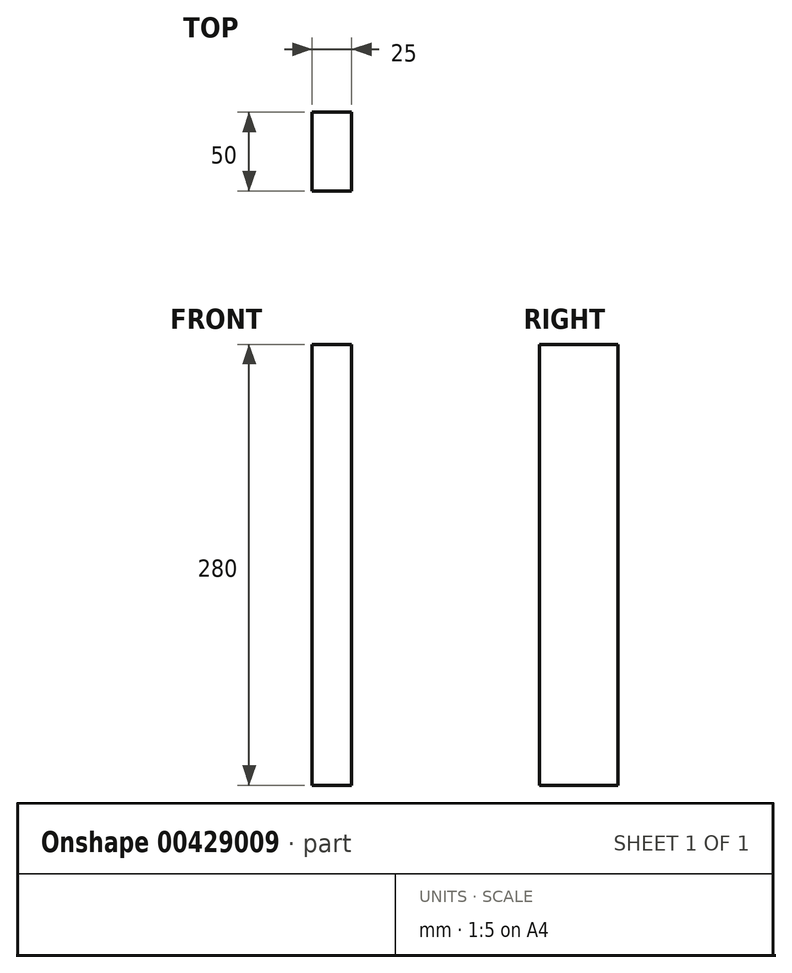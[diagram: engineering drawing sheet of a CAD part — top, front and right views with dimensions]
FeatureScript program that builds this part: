
annotation { "Feature Type Name" : "Feature", "Feature Type Description" : "" }
export const myFeature = defineFeature(function(context is Context, id is Id, definition is map)
    precondition{}
    {
        {
            var Q0;
            Q0=qCreatedBy(makeId("Right.planeOp"),FACE);
            var sketch = newSketch(context, id + "F0", { "sketchPlane" : qUnion([Q0])});
            skLineSegment(sketch, "E0.bottom", {"start": v(25, -140) * mm, "end": v(-25, -140) * mm});
            skLineSegment(sketch, "E0.top", {"start": v(25, 140) * mm, "end": v(-25, 140) * mm});
            skLineSegment(sketch, "E0.left", {"start": v(25, -140) * mm, "end": v(25, 140) * mm});
            skLineSegment(sketch, "E0.right", {"start": v(-25, -140) * mm, "end": v(-25, 140) * mm});
            skPoint(sketch, "E0.middle", {"position": v(0, 0) * mm});
            skSolve(sketch);
        }
        {
            var Q0;
            Q0=makeQuery(id+"F0.imprint","IMPRINT",FACE,{"disambiguationData":[TD([[makeQuery(id+"F0.imprint","IMPRINT",EDGE,{"derivedFrom":sQuery(id+"F0.wireOp",EDGE,"E0.bottom")}),-1.0]])]});
            extrude(context, id + "F1", {"entities" : qUnion([Q0]), "depth" : 25 * mm});
        }
    });
